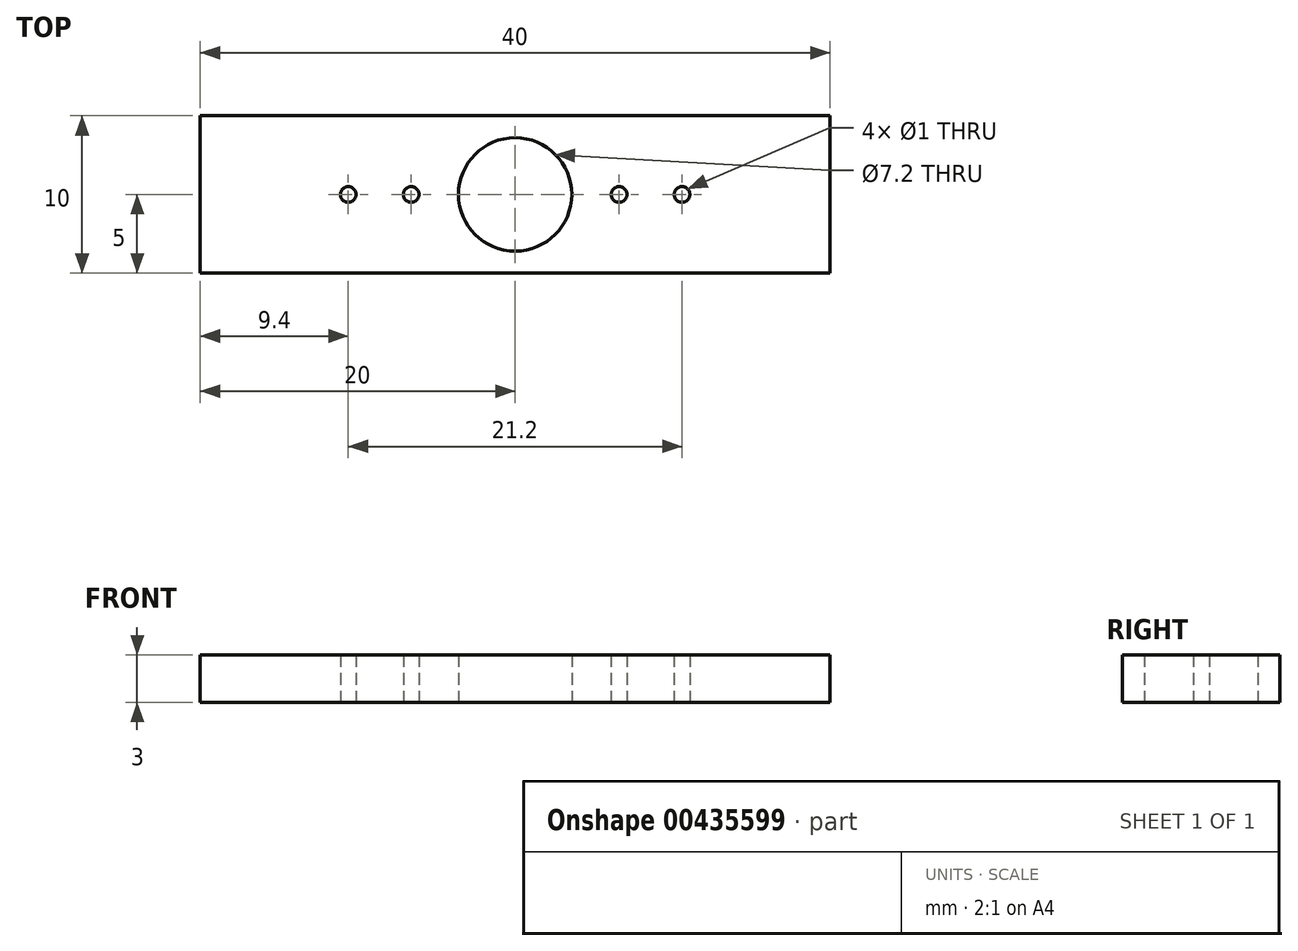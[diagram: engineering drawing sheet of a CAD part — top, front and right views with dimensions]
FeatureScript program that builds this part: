
annotation { "Feature Type Name" : "Feature", "Feature Type Description" : "" }
export const myFeature = defineFeature(function(context is Context, id is Id, definition is map)
    precondition{}
    {
        {
            var Q0;
            Q0=qCreatedBy(makeId("Top.planeOp"),FACE);
            var sketch = newSketch(context, id + "F0", { "sketchPlane" : qUnion([Q0])});
            skLineSegment(sketch, "E0.bottom", {"start": v(20, 5) * mm, "end": v(-20, 5) * mm});
            skLineSegment(sketch, "E0.top", {"start": v(20, -5) * mm, "end": v(-20, -5) * mm});
            skLineSegment(sketch, "E0.left", {"start": v(20, 5) * mm, "end": v(20, -5) * mm});
            skLineSegment(sketch, "E0.right", {"start": v(-20, 5) * mm, "end": v(-20, -5) * mm});
            skPoint(sketch, "E0.middle", {"position": v(0, 0) * mm});
            skCircle(sketch, "E1", {"center": v(0, 0) * mm, "radius": 3.6 * mm});
            skCircle(sketch, "E2", {"center": v(-6.6, 0) * mm, "radius": 0.5 * mm});
            skCircle(sketch, "E3", {"center": v(-10.6, 0) * mm, "radius": 0.5 * mm});
            skCircle(sketch, "E4.MirrorC", {"center": v(6.6, 0) * mm, "radius": 0.5 * mm});
            skCircle(sketch, "E5.MirrorC", {"center": v(10.6, 0) * mm, "radius": 0.5 * mm});
            skSolve(sketch);
        }
        {
            var Q0;
            Q0=makeQuery(id+"F0.imprint","IMPRINT",FACE,{"disambiguationData":[TD([[makeQuery(id+"F0.imprint","IMPRINT",EDGE,{"derivedFrom":sQuery(id+"F0.wireOp",EDGE,"E0.bottom")}),1.0]])]});
            extrude(context, id + "F1", {"entities" : qUnion([Q0]), "endBound" : BoundingType.SYMMETRIC, "depth" : 3 * mm});
        }
    });
